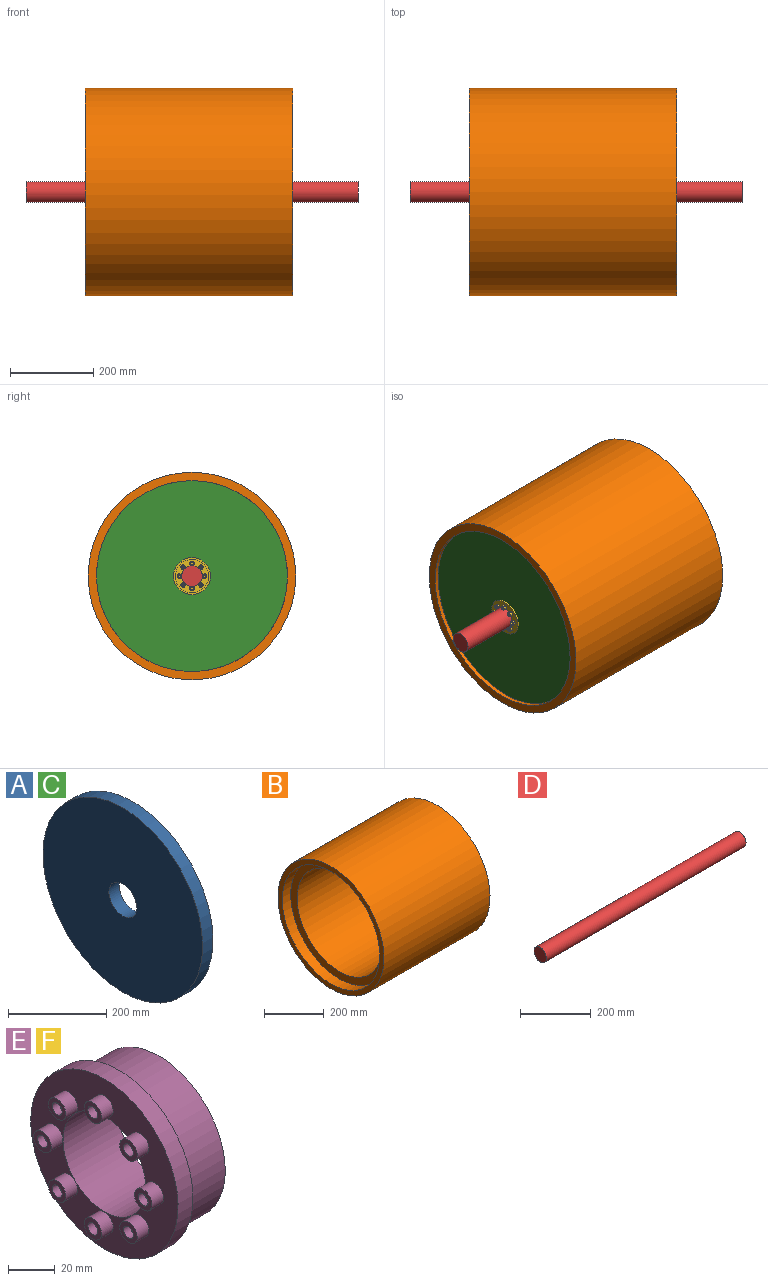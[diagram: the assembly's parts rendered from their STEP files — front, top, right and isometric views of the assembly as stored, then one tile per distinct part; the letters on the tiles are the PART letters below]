
ASSEMBLY  parts=6 mates=5
PART A: 4 faces, bbox 30x460x460 mm
  f0: cylinder r=40mm len=80mm, axis (-1,0,0), area 7539.8mm2, adj f2,f3
  f1: cylinder r=230mm len=460mm, axis (-1,0,0), area 43354mm2, adj f2,f3
  f2: plane 460x460mm, normal (1,0,0), area 161163.7mm2, adj f0,f1
  f3: plane 460x460mm, normal (-1,0,0), area 161163.7mm2, adj f0,f1
PART B: 8 faces, bbox 500x500x500 mm
  f0: cylinder r=230mm len=460mm, axis (-1,0,0), area 57805.3mm2, adj f3,f7
  f1: plane 500x500mm, normal (1,0,0), area 30159.3mm2, adj f2,f4
  f2: cylinder r=250mm len=500mm, axis (-1,0,0), area 785398.2mm2, adj f1,f3
  f3: plane 500x500mm, normal (-1,0,0), area 30159.3mm2, adj f0,f2
  f4: cylinder r=230mm len=460mm, axis (-1,0,0), area 57805.3mm2, adj f1,f6
  f5: cylinder r=200mm len=420mm, axis (-1,0,0), area 527787.6mm2, adj f6,f7
  f6: plane 460x460mm, normal (1,0,0), area 40526.5mm2, adj f4,f5
  f7: plane 460x460mm, normal (-1,0,0), area 40526.5mm2, adj f0,f5
PART C: same geometry as A
PART D: 3 faces, bbox 800x50x50 mm
  f0: cylinder r=25mm len=800mm, axis (-1,0,0), area 125663.7mm2, adj f1,f2
  f1: plane 50x50mm, normal (1,0,0), area 1963.5mm2, adj f0
  f2: plane 50x50mm, normal (-1,0,0), area 1963.5mm2, adj f0
PART E: 38 faces, bbox 40x89x89 mm
  f0: cylinder r=25mm len=50mm, axis (-1,0,0), area 5183.6mm2, adj f2,f4
  f1: cylinder r=40mm len=80mm, axis (-1,0,0), area 6031.9mm2, adj f2,f5
  f2: plane 80x80mm, normal (1,0,0), area 3063.1mm2, adj f0,f1
  f3: cylinder r=44.5mm len=89mm, axis (1,0,0), area 2516.4mm2, adj f4,f5
  f4: plane 89x89mm, normal (-1,0,0), area 3557mm2, adj f0,f3,f6,f10,f14,f18,f22,f26
  f5: plane 89x89mm, normal (1,0,0), area 1194.6mm2, adj f1,f3
  f6: cylinder r=5.28mm len=10.56mm, axis (1,0,0), area 232.2mm2, adj f4,f7
  f7: plane 10.56x10.56mm, normal (-1,0,0), area 59.9mm2, adj f6,f8
  f8: cylinder r=2.97mm len=5.94mm, axis (-1,0,0), area 74.6mm2, adj f7,f9
  f9: plane 5.94x5.94mm, normal (-1,0,0), area 27.7mm2, adj f8
  f10: cylinder r=5.28mm len=10.56mm, axis (1,0,0), area 232.2mm2, adj f4,f11
  f11: plane 10.56x10.56mm, normal (-1,0,0), area 59.9mm2, adj f10,f12
  f12: cylinder r=2.97mm len=5.94mm, axis (-1,0,0), area 74.6mm2, adj f11,f13
  f13: plane 5.94x5.94mm, normal (-1,0,0), area 27.7mm2, adj f12
  f14: cylinder r=5.28mm len=10.56mm, axis (1,0,0), area 232.2mm2, adj f4,f15
  f15: plane 10.56x10.56mm, normal (-1,0,0), area 59.9mm2, adj f14,f16
  f16: cylinder r=2.97mm len=5.94mm, axis (-1,0,0), area 74.6mm2, adj f15,f17
  f17: plane 5.94x5.94mm, normal (-1,0,0), area 27.7mm2, adj f16
  f18: cylinder r=5.28mm len=10.56mm, axis (1,0,0), area 232.2mm2, adj f4,f19
  f19: plane 10.56x10.56mm, normal (-1,0,0), area 59.9mm2, adj f18,f20
  f20: cylinder r=2.97mm len=5.94mm, axis (-1,0,0), area 74.6mm2, adj f19,f21
  f21: plane 5.94x5.94mm, normal (-1,0,0), area 27.7mm2, adj f20
  f22: cylinder r=5.28mm len=10.56mm, axis (1,0,0), area 232.2mm2, adj f4,f23
  f23: plane 10.56x10.56mm, normal (-1,0,0), area 59.9mm2, adj f22,f24
  f24: cylinder r=2.97mm len=5.94mm, axis (-1,0,0), area 74.6mm2, adj f23,f25
  f25: plane 5.94x5.94mm, normal (-1,0,0), area 27.7mm2, adj f24
  f26: cylinder r=5.28mm len=10.56mm, axis (1,0,0), area 232.2mm2, adj f4,f27
  f27: plane 10.56x10.56mm, normal (-1,0,0), area 59.9mm2, adj f26,f28
  f28: cylinder r=2.97mm len=5.94mm, axis (-1,0,0), area 74.6mm2, adj f27,f29
  f29: plane 5.94x5.94mm, normal (-1,0,0), area 27.7mm2, adj f28
  f30: cylinder r=5.28mm len=10.56mm, axis (1,0,0), area 232.2mm2, adj f4,f31
  f31: plane 10.56x10.56mm, normal (-1,0,0), area 59.9mm2, adj f30,f32
  f32: cylinder r=2.97mm len=5.94mm, axis (-1,0,0), area 74.6mm2, adj f31,f33
  f33: plane 5.94x5.94mm, normal (-1,0,0), area 27.7mm2, adj f32
  f34: cylinder r=5.28mm len=10.56mm, axis (1,0,0), area 232.2mm2, adj f4,f35
  f35: plane 10.56x10.56mm, normal (-1,0,0), area 59.9mm2, adj f34,f36
  f36: cylinder r=2.97mm len=5.94mm, axis (-1,0,0), area 74.6mm2, adj f35,f37
  f37: plane 5.94x5.94mm, normal (-1,0,0), area 27.7mm2, adj f36
PART F: same geometry as E
PLACE A rot(axis=(-1,0,0),180deg) t=(603,0,0)mm
PLACE B rot(axis=(-1,0,0),180deg) t=(393,0,0)mm
PLACE C rot(axis=(-1,0,0),90deg) t=(153,0,0)mm
PLACE D at identity
PLACE E rot(axis=(0,0,1),180deg) t=(627,0,0)mm
PLACE F rot(axis=(1,0,0),180deg) t=(159,0,0)mm
MATE fastened E.f0 <-> A.f0  axis (1,0,0) through (603,0,0)mm
MATE fastened C.f0 <-> F.f0  axis (1,0,0) through (183,0,0)mm
MATE fastened B.f0 <-> E.f0  axis (1,0,0) through (603,0,0)mm
MATE cylindrical F.f0 <-> D.f0  axis (-1,0,0) through (150,0,0)mm
MATE fastened B.f5 <-> C.f1  axis (-1,0,0) through (183,0,0)mm
